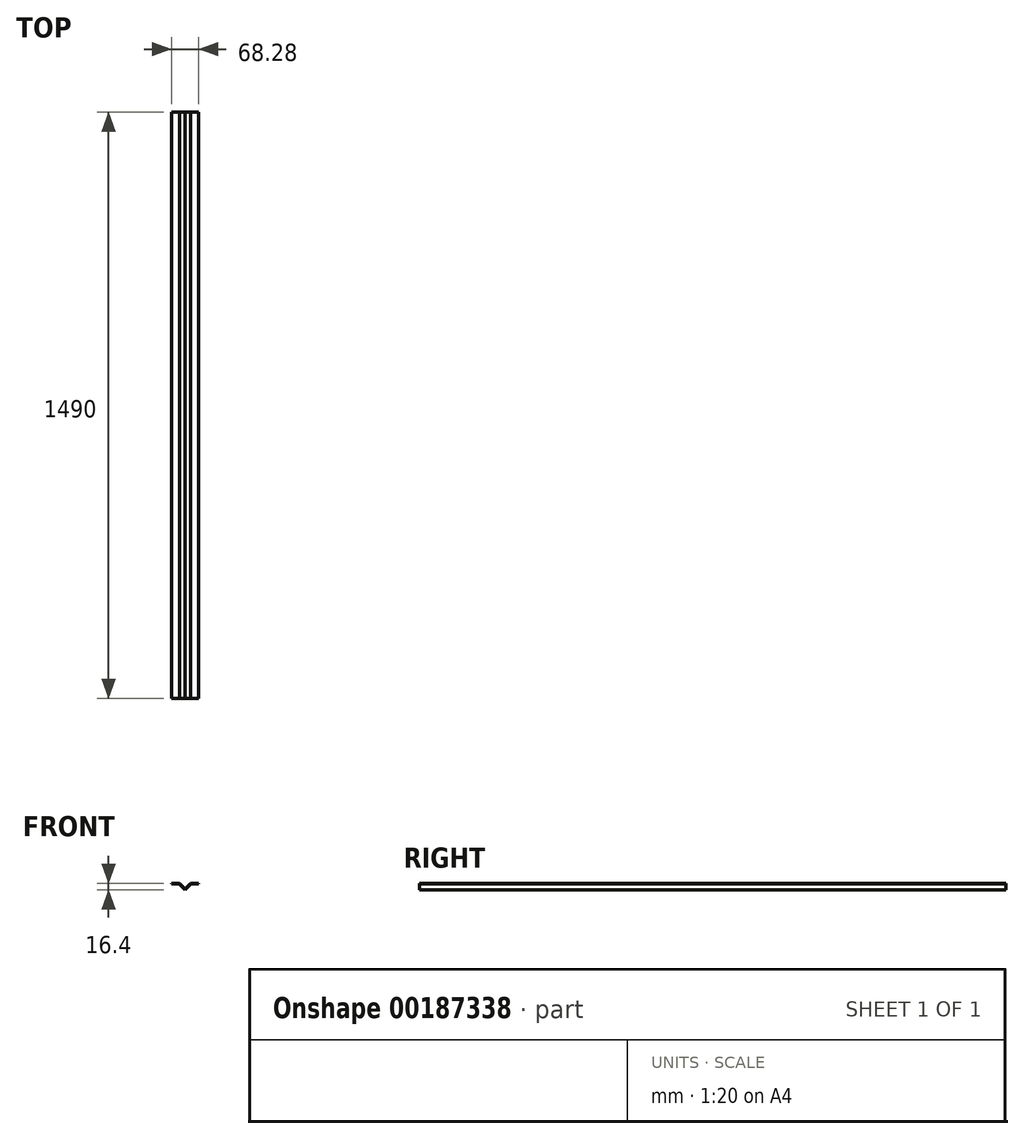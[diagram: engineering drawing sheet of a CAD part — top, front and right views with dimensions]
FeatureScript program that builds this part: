
annotation { "Feature Type Name" : "Feature", "Feature Type Description" : "" }
export const myFeature = defineFeature(function(context is Context, id is Id, definition is map)
    precondition{}
    {
        {
            var Q0;
            Q0=qCreatedBy(makeId("Front.planeOp"),FACE);
            var sketch = newSketch(context, id + "F0", { "sketchPlane" : qUnion([Q0])});
            skLineSegment(sketch, "E0", {"start": v(-34.14, 0) * mm, "end": v(-14.14, 0) * mm});
            skLineSegment(sketch, "E1", {"start": v(14.14, 0) * mm, "end": v(34.14, 0) * mm});
            skLineSegment(sketch, "E2", {"start": v(-14.14, 0) * mm, "end": v(0, -14.14) * mm});
            skLineSegment(sketch, "E3", {"start": v(0, -14.14) * mm, "end": v(14.14, 0) * mm});
            skLineSegment(sketch, "E4.0", {"start": v(14.8, -1.6) * mm, "end": v(34.14, -1.6) * mm});
            skLineSegment(sketch, "E4.1", {"start": v(0, -16.4) * mm, "end": v(14.8, -1.6) * mm});
            skLineSegment(sketch, "E4.2", {"start": v(-14.8, -1.6) * mm, "end": v(0, -16.4) * mm});
            skLineSegment(sketch, "E4.3", {"start": v(-34.14, -1.6) * mm, "end": v(-14.8, -1.6) * mm});
            skLineSegment(sketch, "E5", {"start": v(-34.14, 0) * mm, "end": v(-34.14, -1.6) * mm});
            skLineSegment(sketch, "E6", {"start": v(34.14, 0) * mm, "end": v(34.14, -1.6) * mm});
            skSolve(sketch);
        }
        {
            var Q0;
            Q0=qSketchRegion(id+"F0",true);
            extrude(context, id + "F1", {"entities" : qUnion([Q0]), "endBound" : BoundingType.SYMMETRIC, "depth" : 1490 * mm});
        }
    });
